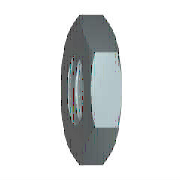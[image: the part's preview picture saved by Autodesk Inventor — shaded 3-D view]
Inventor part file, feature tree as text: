
AUTODESK INVENTOR PART (.ipt)
format: ipt  version: 2023.1 (Build 271208000, 208)  size: 178,688 bytes
history: native  units: mm (DEFAULTED — no unit token found)
features: sketch x3, chamfer x1, hole x1, other x1, plane x1
ambient origin geometry x7: Origin, YZ Plane, XZ Plane, X Axis, Y Axis, Z Axis, Center Point
bodies: Solid1 (feature_tree), Body (feature_tree)
feature tree (7):
  chamfer  "Chamfer1"  Angle=30.0deg  [1 undecoded]
  hole  "Thread"  [1 undecoded]
  other  "Work Axis1"
  plane  "Work Plane1"
  sketch  "Sketch1"  dims[d0=6.350853mm]
  sketch  "Sketch2"  dims[d1=1.8mm]
  sketch  "Sketch3"  dims[d2=0.0mm d3=30.0deg d4=30.0deg d5=4.6mm d6=4.6mm d7=90.0deg d25=2.459mm d26=6.0mm d27=4.0mm d28=2.0mm d29=14.3117mm d30=8.0mm d31=20.594885mm d8=0.270633mm d9=30.0deg d10=0.270633mm d11=30.0deg d13=0.0mm d14=0.0mm d39=0.0mm d40=0.270633mm d41=0.270633mm d42=0.0mm]
note: 2 required parameter values undecoded (feature->parameter linkage not recoverable at this tier; creation-order binding heuristic only, values carry confidence <= 0.55)
